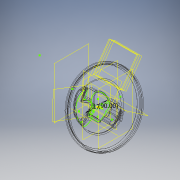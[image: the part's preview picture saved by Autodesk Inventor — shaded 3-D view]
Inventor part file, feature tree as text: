
AUTODESK INVENTOR PART (.ipt)
format: ipt  version: 2018 (Build 220112000, 112)  size: 3,852,288 bytes
history: native  units: mm
features: sketch x143, extrude x128, fillet x64, plane x15, revolve x4, hole x1, direct_edit x1, other x1
ambient origin geometry x8: Origin, YZ Plane, XZ Plane, XY Plane, X Axis, Y Axis, Z Axis, Center Point
bodies: Body1 (feature_tree)
feature tree (357):
  plane  "Work Plane5"
  sketch  "Sketch28"  dims[d118=18.7mm d119=0.0mm d120=0.9mm d121=0.0mm]
  extrude  "Extrusion21"  Depth=0.9mm TaperAngle=0.0deg
  plane  "Work Plane4"
  extrude  "Extrusion22"  Depth=3.8mm
  extrude  "Extrusion23"  Depth=46.7mm
  plane  "Work Plane3"
  hole  "Hole6"  [1 undecoded]
  extrude  "Extrusion27"  Depth=3.8mm
  extrude  "Extrusion28"  Depth=32.03mm
  extrude  "Extrusion30"  Depth=10.0mm TaperAngle=0.0deg
  extrude  "Extrusion31"  Depth=16.3mm TaperAngle=0.0deg
  sketch  "Sketch56"  dims[d188=16.3mm d189=0.0mm d190=16.3mm d191=0.0mm]
  sketch  "Sketch57"  dims[d192=16.3mm d193=0.0mm d194=16.3mm d195=0.0mm]
  extrude  "Extrusion33"  Depth=16.3mm TaperAngle=0.0deg
  extrude  "Extrusion34"  Depth=16.3mm TaperAngle=0.0deg
  extrude  "Extrusion35"  Depth=15.9mm TaperAngle=0.0deg
  extrude  "Extrusion36"  Depth=15.9mm TaperAngle=0.0deg
  extrude  "Extrusion37"  TaperAngle=90.0deg  [1 undecoded]
  extrude  "Extrusion38"  TaperAngle=0.0deg  [1 undecoded]
  extrude  "Extrusion39"  Depth=0.2mm TaperAngle=0.0deg
  extrude  "Extrusion40"  Depth=3.17mm
  extrude  "Extrusion41"  Depth=6.1mm
  sketch  "Sketch68"  dims[d251=10.0mm d252=0.0mm d253=3.91mm d254=0.0mm]
  sketch  "Sketch69"  dims[d255=0.0mm d256=0.0mm d257=3.91mm d258=0.0mm]
  extrude  "Extrusion42"  Depth=0.8mm TaperAngle=0.0deg
  extrude  "Extrusion43"  TaperAngle=0.0deg  [1 undecoded]
  extrude  "Extrusion45"  Depth=10.0mm TaperAngle=0.0deg
  extrude  "Extrusion47"  Depth=3.91mm TaperAngle=0.0deg
  extrude  "Extrusion48"  Depth=0.6mm TaperAngle=0.0deg
  extrude  "Extrusion49"  Depth=0.199mm
  direct_edit  "Direct Edit3"
  extrude  "Extrusion51"  TaperAngle=0.0deg  [1 undecoded]
  extrude  "Extrusion52"  Depth=0.7mm TaperAngle=0.0deg
  extrude  "Extrusion53"  Depth=0.09mm TaperAngle=0.0deg
  extrude  "Extrusion54"  TaperAngle=0.0deg  [1 undecoded]
  extrude  "Extrusion55"  Depth=3.9mm TaperAngle=0.0deg
  extrude  "Extrusion60"  TaperAngle=0.0deg  [1 undecoded]
  extrude  "Extrusion61"  Depth=0.657mm
  extrude  "Extrusion62"  Depth=10.0mm TaperAngle=0.0deg
  fillet  "Fillet13"  Radius=10.0mm
  extrude  "Extrusion64"  TaperAngle=0.0deg  [1 undecoded]
  extrude  "Extrusion65"  TaperAngle=0.0deg  [1 undecoded]
  extrude  "Extrusion66"  Depth=0.253mm
  extrude  "Extrusion67"  TaperAngle=0.0deg  [1 undecoded]
  fillet  "Fillet14"  [1 undecoded]
  extrude  "Extrusion68"  Depth=15.0mm
  extrude  "Extrusion69"  Depth=22.68928mm
  extrude  "Extrusion70"  TaperAngle=90.0deg  [1 undecoded]
  fillet  "Fillet15"  [1 undecoded]
  extrude  "Extrusion71"  TaperAngle=90.0deg  [1 undecoded]
  extrude  "Extrusion72"  Depth=3.490659mm
  extrude  "Extrusion73"  Depth=2.0mm TaperAngle=0.0deg
  extrude  "Extrusion74"  TaperAngle=0.0deg  [1 undecoded]
  fillet  "Fillet16"  Radius=10.0mm
  fillet  "Fillet17"  Radius=0.22mm
  extrude  "Extrusion75"  Depth=5.0mm TaperAngle=0.0deg
  plane  "Work Plane6"
  extrude  "Extrusion78"  Depth=10.0mm TaperAngle=0.0deg
  extrude  "Extrusion79"  Depth=10.0mm TaperAngle=0.0deg
  extrude  "Extrusion80"  Depth=10.0mm TaperAngle=0.0deg
  extrude  "Extrusion81"  Depth=10.0mm TaperAngle=0.0deg
  extrude  "Extrusion82"  Depth=5.99mm
  fillet  "Fillet18"  [1 undecoded]
  fillet  "Fillet19"  Radius=5.99mm
  fillet  "Fillet20"  Radius=1.49mm
  extrude  "Extrusion83"  Depth=1.77mm
  extrude  "Extrusion84"  Depth=10.0mm TaperAngle=0.0deg
  fillet  "Fillet21"  Radius=4.0mm
  extrude  "Extrusion87"  Depth=4.0mm TaperAngle=0.0deg
  plane  "Work Plane7"
  extrude  "Extrusion88"  TaperAngle=0.0deg  [1 undecoded]
  extrude  "Extrusion89"  Depth=7.0mm TaperAngle=0.0deg
  extrude  "Extrusion90"  Depth=10.0mm TaperAngle=0.0deg
  extrude  "Extrusion91"  Depth=7.0mm TaperAngle=0.0deg
  fillet  "Fillet27"  Radius=7.0mm
  extrude  "Extrusion93"  Depth=7.0mm TaperAngle=0.0deg
  extrude  "Extrusion94"  Depth=1.7mm TaperAngle=0.0deg
  fillet  "Fillet29"  [1 undecoded]
  extrude  "Extrusion95"  Depth=10.0mm TaperAngle=0.0deg
  extrude  "Extrusion97"  Depth=10.0mm TaperAngle=0.0deg
  extrude  "Extrusion98"  Depth=1.0mm TaperAngle=0.0deg
  extrude  "Extrusion99"  Depth=15.687mm
  extrude  "Extrusion100"  Depth=9.4mm
  extrude  "Extrusion101"  TaperAngle=90.0deg  [1 undecoded]
  extrude  "Extrusion102"  Depth=10.0mm TaperAngle=0.0deg
  extrude  "Extrusion104"  Depth=50.0mm TaperAngle=0.0deg
  fillet  "Fillet30"  Radius=50.0mm
  extrude  "Extrusion106"  Depth=10.0mm TaperAngle=0.0deg
  fillet  "Fillet33"  Radius=32.0mm
  fillet  "Fillet34"  Radius=9.4mm
  fillet  "Fillet35"  [1 undecoded]
  fillet  "Fillet38"  Radius=10.0mm
  extrude  "Extrusion108"  Depth=10.0mm TaperAngle=0.0deg
  extrude  "Extrusion109"  Depth=10.0mm TaperAngle=0.0deg
  extrude  "Extrusion110"  TaperAngle=0.0deg  [1 undecoded]
  extrude  "Extrusion111"  Depth=18.0mm TaperAngle=0.0deg
  extrude  "Extrusion112"  Depth=2.0mm
  sketch  "Sketch146"  dims[d571=2.0mm d572=2.0mm]
  extrude  "Extrusion113"  Depth=2.0mm
  extrude  "Extrusion114"  Depth=2.0mm
  extrude  "Extrusion115"  Depth=2.0mm
  extrude  "Extrusion116"  Depth=2.0mm
  extrude  "Extrusion118"  Depth=2.0mm
  sketch  "Sketch154"  dims[d590=2.0mm d591=4.0mm]
  extrude  "Extrusion119"  Depth=2.0mm
  extrude  "Extrusion120"  Depth=0.7mm TaperAngle=0.0deg
  extrude  "Extrusion121"  Depth=10.0mm TaperAngle=0.0deg
  extrude  "Extrusion122"  Depth=17.0mm TaperAngle=0.0deg
  extrude  "Extrusion123"  Depth=4.0mm
  extrude  "Extrusion124"  Depth=1.0mm TaperAngle=0.0deg
  extrude  "Extrusion125"  Depth=6.6945mm
  extrude  "Extrusion126"  TaperAngle=0.0deg  [1 undecoded]
  extrude  "Extrusion128"  Depth=15.2mm
  extrude  "Extrusion129"  Depth=26.0mm
  extrude  "Extrusion130"  Depth=28.5mm TaperAngle=0.0deg
  plane  "Work Plane9"
  extrude  "Extrusion133"  Depth=2.0mm
  extrude  "Extrusion134"  Depth=0.567mm
  plane  "Work Plane8"
  extrude  "Extrusion135"  Depth=0.37mm TaperAngle=0.0deg
  plane  "Work Plane2"
  revolve  "Revolution3"  [1 undecoded]
  plane  "Work Plane10"
  extrude  "Extrusion136"  Depth=2.0mm
  extrude  "Extrusion137"  Depth=2.0mm
  extrude  "Extrusion138"  TaperAngle=90.0deg  [1 undecoded]
  extrude  "Extrusion139"  Depth=0.449mm
  sketch  "Sketch184"  dims[d657=2.0mm d658=1.2mm d659=0.0mm]
  plane  "Work Plane11"
  extrude  "Extrusion140"  Depth=0.526mm
  extrude  "Extrusion141"  [1 undecoded]
  extrude  "Extrusion142"  [1 undecoded]
  extrude  "Extrusion143"  Depth=2.0mm
  revolve  "Revolution4"  [1 undecoded]
  extrude  "Extrusion145"  Depth=1.2mm TaperAngle=0.0deg
  sketch  "Sketch192"  dims[d671=0.7mm d672=0.0mm d673=2.0mm]
  extrude  "Extrusion147"  Depth=2.0mm
  extrude  "Extrusion148"  Depth=2.0mm
  extrude  "Extrusion149"  Depth=2.0mm
  sketch  "Sketch198"
  sketch  "Sketch199"
  sketch  "Sketch200"
  extrude  "Extrusion150"  Depth=2.3mm TaperAngle=0.0deg
  sketch  "Sketch201"
  sketch  "Sketch202"
  extrude  "Extrusion151"  Depth=2.0mm
  extrude  "Extrusion152"  Depth=2.0mm
  extrude  "Extrusion153"  Depth=2.0mm
  extrude  "Extrusion154"  Depth=2.0mm
  sketch  "Sketch207"
  extrude  "Extrusion155"  Depth=0.473mm TaperAngle=0.0deg
  fillet  "Fillet39"  Radius=2.0mm
  fillet  "Fillet40"  Radius=2.0mm
  fillet  "Fillet41"  Radius=0.473mm
  fillet  "Fillet42"  Radius=1.0mm
  fillet  "Fillet43"  Radius=1.0mm
  fillet  "Fillet44"  [1 undecoded]
  fillet  "Fillet45"  [1 undecoded]
  fillet  "Fillet46"  [1 undecoded]
  fillet  "Fillet47"  [1 undecoded]
  plane  "Work Plane12"
  extrude  "Extrusion156"  [1 undecoded]
  fillet  "Fillet48"  [1 undecoded]
  fillet  "Fillet49"  [1 undecoded]
  fillet  "Fillet50"  [1 undecoded]
  fillet  "Fillet51"  [1 undecoded]
  extrude  "Extrusion157"  [1 undecoded]
  fillet  "Fillet52"  [1 undecoded]
  extrude  "Extrusion158"  [1 undecoded]
  extrude  "Extrusion159"  [1 undecoded]
  extrude  "Extrusion161"  [1 undecoded]
  fillet  "Fillet53"  [1 undecoded]
  plane  "Work Plane13"
  extrude  "Extrusion163"  [1 undecoded]
  extrude  "Extrusion164"  [1 undecoded]
  extrude  "Extrusion166"  [1 undecoded]
  extrude  "Extrusion167"  [1 undecoded]
  revolve  "Revolution5"  [1 undecoded]
  extrude  "Extrusion168"  [1 undecoded]
  fillet  "Fillet54"  [1 undecoded]
  fillet  "Fillet55"  [1 undecoded]
  extrude  "Extrusion169"  [1 undecoded]
  sketch  "Sketch220"
  fillet  "Fillet56"  [1 undecoded]
  fillet  "Fillet57"  [1 undecoded]
  extrude  "Extrusion171"  [1 undecoded]
  extrude  "Extrusion172"  [1 undecoded]
  fillet  "Fillet58"  [1 undecoded]
  fillet  "Fillet59"  [1 undecoded]
  fillet  "Fillet60"  [1 undecoded]
  fillet  "Fillet61"  [1 undecoded]
  fillet  "Fillet62"  [1 undecoded]
  fillet  "Fillet63"  [1 undecoded]
  revolve  "Revolution6"  [1 undecoded]
  fillet  "Fillet64"  [1 undecoded]
  extrude  "Extrusion173"  [1 undecoded]
  fillet  "Fillet65"  [1 undecoded]
  fillet  "Fillet66"  [1 undecoded]
  plane  "Work Plane14"
  extrude  "Extrusion174"  [1 undecoded]
  sketch  "Sketch225"
  plane  "Work Plane15"
  extrude  "Extrusion176"  [1 undecoded]
  fillet  "Fillet67"  [1 undecoded]
  fillet  "Fillet68"  [1 undecoded]
  fillet  "Fillet69"  [1 undecoded]
  fillet  "Fillet70"  [1 undecoded]
  extrude  "Extrusion177"  [1 undecoded]
  fillet  "Fillet71"  [1 undecoded]
  fillet  "Fillet72"  [1 undecoded]
  fillet  "Fillet73"  [1 undecoded]
  fillet  "Fillet74"  [1 undecoded]
  fillet  "Fillet75"  [1 undecoded]
  fillet  "Fillet76"  [1 undecoded]
  fillet  "Fillet77"  [1 undecoded]
  sketch  "Sketch228"
  extrude  "Extrusion178"  [1 undecoded]
  fillet  "Fillet78"  [1 undecoded]
  fillet  "Fillet79"  [1 undecoded]
  extrude  "Extrusion179"  [1 undecoded]
  fillet  "Fillet80"  [1 undecoded]
  extrude  "Extrusion180"  [1 undecoded]
  fillet  "Fillet81"  [1 undecoded]
  fillet  "Fillet82"  [1 undecoded]
  fillet  "Fillet83"  [1 undecoded]
  plane  "Work Plane16"
  extrude  "Extrusion181"  [1 undecoded]
  fillet  "Fillet84"  [1 undecoded]
  fillet  "Fillet85"  [1 undecoded]
  fillet  "Fillet86"  [1 undecoded]
  sketch  "Sketch41"  dims[d122=0.7mm d123=0.0mm d128=3.8mm]
  sketch  "Sketch42"  dims[d129=3.8mm d130=46.7mm]
  sketch  "Sketch43"  dims[d134=3.8mm d135=4.369mm d136=5.824mm d137=2.0mm d138=14.3117mm d139=6.637mm d140=0.0mm d150=1.5mm d151=0.0mm]
  sketch  "Sketch50"  dims[d152=1.2mm d153=0.0mm d159=3.8mm]
  sketch  "Sketch51"  dims[d161=3.8mm d168=23.3333mm d173=32.03mm]
  sketch  "Sketch53"  dims[d174=16.015mm d175=10.0mm d176=0.0mm]
  sketch  "Sketch54"  dims[d179=0.0mm d180=0.0mm d186=16.3mm d187=0.0mm]
  sketch  "Sketch58"  dims[d196=15.9mm d197=0.0mm d198=15.9mm d199=0.0mm]
  sketch  "Sketch60"  dims[d200=15.9mm d201=0.0mm d202=15.9mm d203=0.0mm]
  sketch  "Sketch61"  dims[d209=17.0mm d210=90.0deg]
  sketch  "Sketch62"  dims[d211=6.0mm d212=0.0mm d213=0.0mm d214=0.0mm]
  sketch  "Sketch63"  dims[d225=6.0mm d226=0.0mm d230=0.2mm d231=0.0mm]
  sketch  "Sketch64"  dims[d232=3.17mm d233=3.17mm]
  sketch  "Sketch65"  dims[d235=19.4mm d236=6.1mm]
  sketch  "Sketch66"  dims[d237=0.8mm d238=0.0mm d239=0.8mm d240=0.0mm]
  sketch  "Sketch67"  dims[d246=9.0mm d247=10.0mm d248=10.0mm d249=0.0mm d250=0.0mm]
  sketch  "Sketch70"  dims[d267=0.0mm d268=0.0mm d269=0.6mm d270=0.0mm]
  sketch  "Sketch72"  dims[d271=0.0mm d272=0.0mm d273=0.199mm]
  sketch  "Sketch74"  dims[d276=0.0mm d277=0.0mm d278=0.0mm d279=0.0mm]
  sketch  "Sketch75"  dims[d280=0.7mm d281=0.0mm d282=0.7mm d283=0.0mm]
  sketch  "Sketch76"  dims[d284=3.64mm d285=0.09mm d286=0.0mm]
  sketch  "Sketch79"  dims[d287=0.09mm d288=0.0mm d289=0.0mm d290=0.0mm]
  sketch  "Sketch80"  dims[d291=0.356mm d292=3.9mm d293=0.0mm]
  sketch  "Sketch81"  dims[d294=3.9mm d295=0.0mm d296=0.0mm d297=0.0mm]
  sketch  "Sketch82"  dims[d298=3.9mm d299=0.0mm d300=0.657mm]
  sketch  "Sketch83"  dims[d301=0.886mm d302=3.9mm d303=0.0mm d313=10.0mm d314=0.0mm]
  sketch  "Sketch89"  dims[d315=10.0mm d316=0.0mm d317=0.0mm d318=0.0mm]
  sketch  "Sketch90"  dims[d319=10.0mm d320=0.0mm d321=0.0mm d322=0.0mm]
  sketch  "Sketch91"  dims[d323=0.467mm d324=0.253mm]
  sketch  "Sketch93"  dims[d325=0.195mm d326=0.0mm d327=0.0mm d328=90.0deg]
  sketch  "Sketch94"  dims[d329=90.0deg d330=15.0mm]
  sketch  "Sketch95"  dims[d332=11.0mm d333=22.68928mm]
  sketch  "Sketch96"  dims[d335=90.0deg d336=90.0deg d337=0.0mm d338=0.0mm]
  sketch  "Sketch97"  dims[d344=0.954mm d350=90.0deg]
  sketch  "Sketch98"  dims[d351=3.490659mm d352=3.490659mm]
  sketch  "Sketch99"  dims[d353=6.0mm d354=0.0mm d363=2.0mm d364=0.0mm]
  sketch  "Sketch100"  dims[d365=2.0mm d366=0.0mm d374=0.0mm d375=0.0mm d376=10.0mm d377=0.0mm d378=0.22mm]
  sketch  "Sketch101"  dims[d381=5.0mm d382=0.0mm d383=5.0mm d384=0.0mm]
  sketch  "Sketch102"  dims[d386=3.8mm d397=10.0mm d398=0.0mm]
  sketch  "Sketch103"  dims[d401=0.3mm d402=0.0mm d403=10.0mm d404=0.0mm]
  sketch  "Sketch104"  dims[d405=10.0mm d406=0.0mm d407=10.0mm d408=0.0mm]
  sketch  "Sketch106"  dims[d409=10.0mm d410=0.0mm d411=10.0mm d412=0.0mm]
  sketch  "Sketch107"  dims[d415=10.0mm d416=0.0mm d419=0.865mm d421=0.0mm d422=0.0mm d424=5.99mm d425=1.49mm]
  sketch  "Sketch108"  dims[d426=0.859mm d431=1.77mm]
  sketch  "Sketch109"  dims[d432=10.0mm d433=0.0mm d434=4.0mm d435=0.0mm d436=4.0mm d437=0.0mm]
  sketch  "Sketch110"  dims[d438=4.0mm d439=0.0mm d440=4.0mm d441=0.0mm]
  sketch  "Sketch113"  dims[d442=0.0mm d443=0.0mm d444=0.0mm d445=0.0mm]
  sketch  "Sketch114"  dims[d446=1.0mm d447=0.0mm d448=7.0mm d449=0.0mm]
  sketch  "Sketch117"  dims[d452=7.0mm d453=0.0mm d454=10.0mm d455=0.0mm]
  sketch  "Sketch118"  dims[d456=0.0mm d457=0.0mm d458=7.0mm d459=0.0mm d460=7.0mm d461=0.0mm]
  sketch  "Sketch119"  dims[d462=0.0mm d463=0.0mm d464=7.0mm d465=0.0mm]
  sketch  "Sketch120"  dims[d466=1.7mm d467=0.0mm d468=1.7mm d469=0.0mm d483=0.0mm d484=0.0mm]
  sketch  "Sketch121"  dims[d485=0.0mm d486=0.0mm d487=10.0mm d488=0.0mm]
  sketch  "Sketch123"  dims[d496=10.0mm d497=0.0mm d498=10.0mm d499=0.0mm]
  sketch  "Sketch124"  dims[d500=31.5mm d501=1.0mm d502=0.0mm]
  sketch  "Sketch126"  dims[d508=-1.0mm d509=15.687mm]
  sketch  "Sketch128"  dims[d510=90.0deg d514=9.4mm]
  sketch  "Sketch129"  dims[d516=7.0mm d519=90.0deg]
  sketch  "Sketch130"  dims[d520=2.75mm d521=0.0mm d522=10.0mm d523=0.0mm]
  sketch  "Sketch131"  dims[d524=7.0mm d525=0.0mm d527=50.0mm d528=0.0mm d529=50.0mm d530=0.0mm]
  sketch  "Sketch132"  dims[d531=50.0mm d532=0.0mm d533=50.0mm d534=0.0mm d535=32.0mm d536=0.0mm d537=9.4mm d538=7.0mm d539=90.0deg d542=10.0mm d543=0.0mm]
  sketch  "Sketch133"  dims[d546=10.0mm d547=0.0mm d548=10.0mm d549=0.0mm]
  sketch  "Sketch135"  dims[d550=31.0mm d551=0.0mm d552=10.0mm d553=0.0mm]
  sketch  "Sketch137"  dims[d554=5.5mm d555=0.0mm d556=0.0mm d557=0.0mm]
  sketch  "Sketch141"  dims[d558=5.5mm d559=0.0mm d560=18.0mm d561=0.0mm]
  sketch  "Sketch142"  dims[d562=18.0mm d563=0.0mm d564=2.0mm]
  sketch  "Sketch143"  dims[d565=2.0mm d566=2.0mm]
  sketch  "Sketch144"  dims[d567=2.0mm d568=2.0mm]
  sketch  "Sketch145"  dims[d569=2.0mm d570=2.0mm]
  sketch  "Sketch147"  dims[d573=0.0mm d574=0.0mm d575=2.0mm]
  sketch  "Sketch148"  dims[d576=2.0mm d577=2.0mm]
  sketch  "Sketch149"  dims[d578=2.0mm d579=0.7mm d580=0.0mm]
  sketch  "Sketch150"  dims[d581=2.0mm d582=10.0mm d583=0.0mm]
  sketch  "Sketch153"  dims[d584=2.15mm d585=0.0mm d588=17.0mm d589=0.0mm]
  sketch  "Sketch156"  dims[d594=3.0mm d595=0.0mm d596=1.0mm d597=0.0mm]
  sketch  "Sketch157"  dims[d598=7.23mm d599=6.6945mm]
  sketch  "Sketch161"  dims[d602=31.423mm d603=0.0mm d604=0.0mm]
  sketch  "Sketch162"  dims[d605=1.0mm d606=0.0mm d607=15.2mm]
  sketch  "Sketch163"  dims[d609=5.093mm d611=26.0mm]
  sketch  "Sketch164"  dims[d615=90.0deg d616=28.5mm d617=0.0mm]
  sketch  "Sketch165"  dims[d618=2.0mm d619=2.0mm]
  sketch  "Sketch166"  dims[d620=2.235mm d621=0.0mm d624=0.567mm]
  sketch  "Sketch169"  dims[d625=0.682mm d626=0.37mm d627=0.0mm]
  sketch  "Sketch170"  dims[d628=1.2mm d629=0.0mm d630=2.0mm]
  sketch  "Sketch171"  dims[d631=2.0mm d632=2.0mm]
  sketch  "Sketch174"  dims[d633=2.0mm d634=2.0mm]
  sketch  "Sketch175"  dims[d635=2.0mm d639=90.0deg]
  sketch  "Sketch176"  dims[d640=90.0deg d641=0.449mm]
  sketch  "Sketch179"  dims[d642=1.2mm d643=0.0mm d644=0.526mm]
  sketch  "Sketch180"  dims[d645=2.0mm d646=-23.0mm]
  sketch  "Sketch181"  dims[d647=18.0mm d648=0.0mm d651=-2.2mm]
  sketch  "Sketch182"  dims[d652=1.4mm d653=0.0mm d654=2.0mm]
  sketch  "Sketch183"  dims[d655=2.0mm d656=2.0mm]
  sketch  "Sketch185"  dims[d660=2.0mm d661=2.0mm]
  sketch  "Sketch186"  dims[d662=2.0mm d663=2.0mm]
  sketch  "Sketch187"  dims[d664=2.0mm d665=2.0mm]
  sketch  "Sketch188"  dims[d666=2.0mm d667=2.3mm d668=0.0mm]
  sketch  "Sketch190"  dims[d669=2.0mm d670=2.0mm]
  sketch  "Sketch193"  dims[d674=0.5mm d675=0.0mm d676=2.0mm]
  sketch  "Sketch194"  dims[d677=2.0mm d678=2.0mm]
  sketch  "Sketch195"  dims[d679=12.0mm d680=3.0mm d681=0.0mm d682=2.0mm d683=2.0mm d684=0.473mm d21=1.0mm d22=1.0mm]
  sketch  "Sketch204"
  sketch  "Sketch205"
  sketch  "Sketch206"
  sketch  "Sketch208"
  sketch  "Sketch209"
  sketch  "Sketch210"
  sketch  "Sketch211"
  sketch  "Sketch212"
  sketch  "Sketch213"
  sketch  "Sketch214"
  sketch  "Sketch215"
  sketch  "Sketch216"
  sketch  "Sketch217"
  sketch  "Sketch218"
  sketch  "Sketch219"
  sketch  "Sketch221"
  sketch  "Sketch222"
  sketch  "Sketch223"
  sketch  "Sketch224"
  sketch  "Sketch226"
  sketch  "Sketch227"
  sketch  "Sketch229"
  sketch  "Sketch230"
  sketch  "Sketch231"
  other  "Scale3"
note: 93 required parameter values undecoded (feature->parameter linkage not recoverable at this tier; creation-order binding heuristic only, values carry confidence <= 0.55)